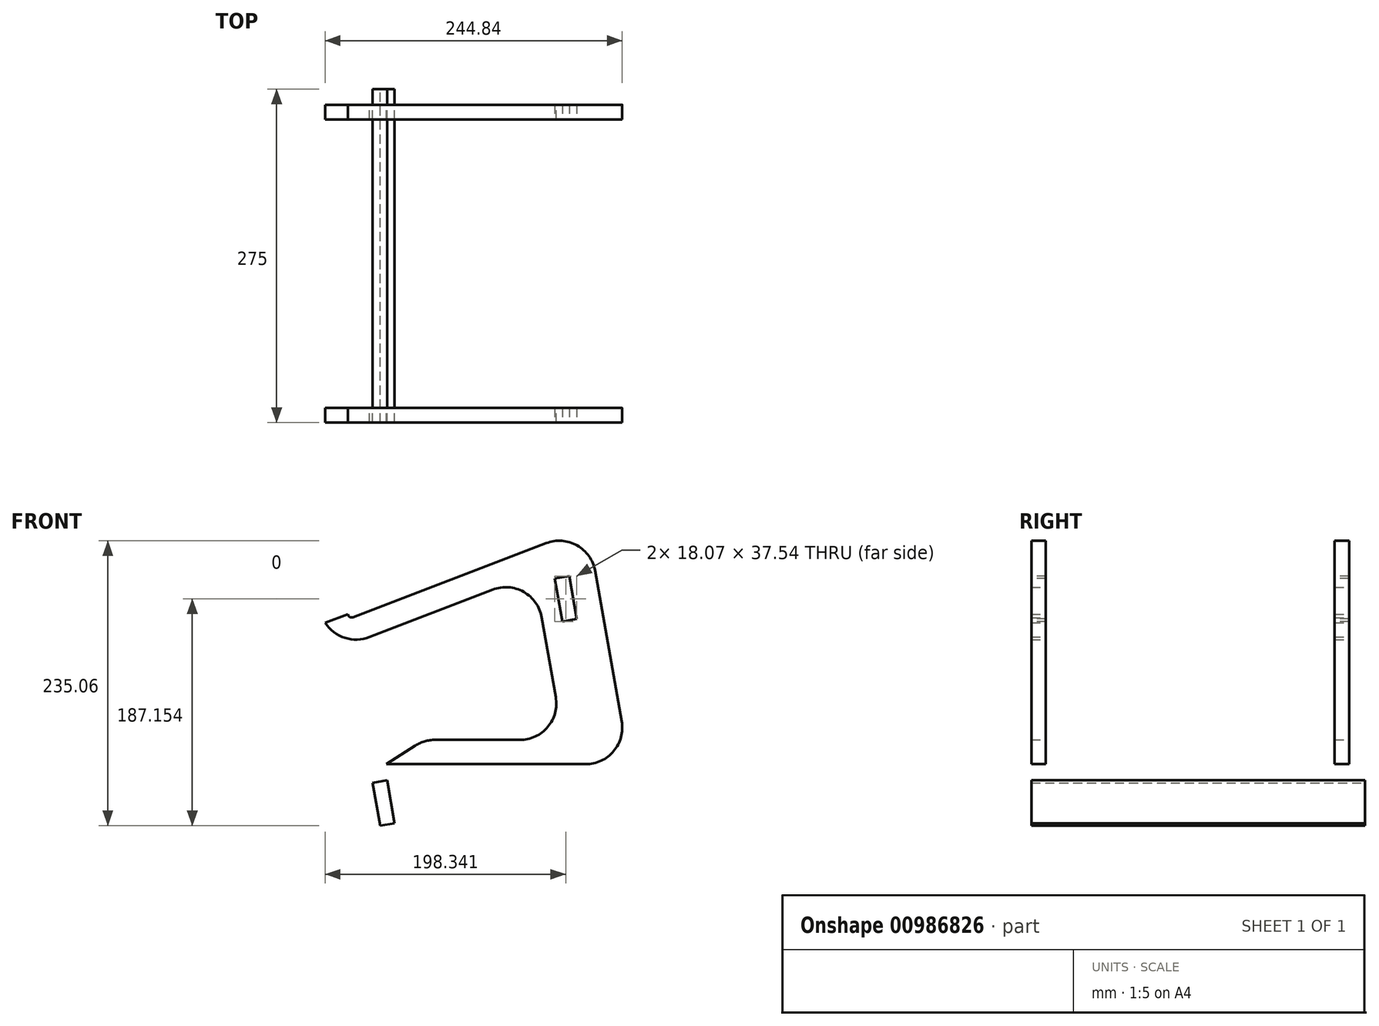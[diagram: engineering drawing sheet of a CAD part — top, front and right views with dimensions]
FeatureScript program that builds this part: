
annotation { "Feature Type Name" : "Feature", "Feature Type Description" : "" }
export const myFeature = defineFeature(function(context is Context, id is Id, definition is map)
    precondition{}
    {
        {
            var Q0;
            Q0=qCreatedBy(makeId("Front.planeOp"),FACE);
            var sketch = newSketch(context, id + "F0", { "sketchPlane" : qUnion([Q0])});
            skLineSegment(sketch, "E0", {"start": v(-177.62, 123.73) * mm, "end": v(-177.26, 122.8) * mm});
            skLineSegment(sketch, "E1", {"start": v(-173.38, 121.08) * mm, "end": v(-14.1, 182.22) * mm});
            skLineSegment(sketch, "E2", {"start": v(26.19, 159.42) * mm, "end": v(48.09, 35.2) * mm});
            skLineSegment(sketch, "E3", {"start": v(18.55, 0) * mm, "end": v(-145.7, 0) * mm});
            skLineSegment(sketch, "E4", {"start": v(-145.7, 0) * mm, "end": v(-121.89, 15.26) * mm});
            skLineSegment(sketch, "E5", {"start": v(-105.7, 20) * mm, "end": v(-35.75, 20) * mm});
            skLineSegment(sketch, "E6", {"start": v(-6.2, 55.2) * mm, "end": v(-17.83, 121.1) * mm});
            skLineSegment(sketch, "E7", {"start": v(-58.12, 143.9) * mm, "end": v(-159.68, 104.91) * mm});
            skPoint(sketch, "E8.visualSharp", {"position": v(-114.49, 20) * mm});
            skArc(sketch, "E8.filletArc", {"start": v(-105.7, 20) * mm, "mid": v(-114.13, 18.8) * mm, "end": v(-121.89, 15.26) * mm});
            skPoint(sketch, "E9.visualSharp", {"position": v(54.3, 0) * mm});
            skArc(sketch, "E9.filletArc", {"start": v(18.55, 0) * mm, "mid": v(41.53, 10.72) * mm, "end": v(48.09, 35.2) * mm});
            skPoint(sketch, "E10.visualSharp", {"position": v(0, 20) * mm});
            skArc(sketch, "E10.filletArc", {"start": v(-35.75, 20) * mm, "mid": v(-12.77, 30.72) * mm, "end": v(-6.2, 55.2) * mm});
            skPoint(sketch, "E11.visualSharp", {"position": v(-24.15, 156.94) * mm});
            skArc(sketch, "E11.filletArc", {"start": v(-17.83, 121.1) * mm, "mid": v(-32.6, 142) * mm, "end": v(-58.12, 143.9) * mm});
            skPoint(sketch, "E12.visualSharp", {"position": v(19.87, 195.26) * mm});
            skArc(sketch, "E12.filletArc", {"start": v(26.19, 159.42) * mm, "mid": v(11.42, 180.32) * mm, "end": v(-14.1, 182.22) * mm});
            skPoint(sketch, "E13.visualSharp", {"position": v(-187.69, 94.16) * mm});
            skPoint(sketch, "E14.visualSharp", {"position": v(-176.18, 120) * mm});
            skArc(sketch, "E14.filletArc", {"start": v(-177.26, 122.8) * mm, "mid": v(-175.68, 121.14) * mm, "end": v(-173.38, 121.08) * mm});
            skLineSegment(sketch, "E15", {"start": v(-196.29, 116.57) * mm, "end": v(-177.62, 123.73) * mm});
            skArc(sketch, "E16", {"start": v(-196.29, 116.57) * mm, "mid": v(-180.1, 104.11) * mm, "end": v(-159.68, 104.91) * mm});
            skSolve(sketch);
        }
        {
            var Q0;
            Q0=qSketchRegion(id+"F0",true);
            extrude(context, id + "F1", {"entities" : qUnion([Q0]), "depth" : 12 * mm, "offsetDistance" : 25 * mm});
        }
        {
            var Q0;
            Q0=makeQuery(id+"F1.opExtrude","CAP_FACE",FACE,{"disambiguationData":[OSD([sQuery(id+"F0.wireOp",EDGE,"E0"),sQuery(id+"F0.wireOp",EDGE,"E1"),sQuery(id+"F0.wireOp",EDGE,"E2"),sQuery(id+"F0.wireOp",EDGE,"E3"),sQuery(id+"F0.wireOp",EDGE,"E4"),sQuery(id+"F0.wireOp",EDGE,"E5"),sQuery(id+"F0.wireOp",EDGE,"E6"),sQuery(id+"F0.wireOp",EDGE,"E7"),sQuery(id+"F0.wireOp",EDGE,"E8.filletArc"),sQuery(id+"F0.wireOp",EDGE,"E9.filletArc"),sQuery(id+"F0.wireOp",EDGE,"E10.filletArc"),sQuery(id+"F0.wireOp",EDGE,"E11.filletArc"),sQuery(id+"F0.wireOp",EDGE,"E12.filletArc"),sQuery(id+"F0.wireOp",EDGE,"E14.filletArc"),sQuery(id+"F0.wireOp",EDGE,"E15"),sQuery(id+"F0.wireOp",EDGE,"E16")])],"isStart":false});
            var sketch = newSketch(context, id + "F2", { "sketchPlane" : qUnion([Q0])});
            skLineSegment(sketch, "E17.bottom", {"start": v(-6.98, 152.99) * mm, "end": v(4.83, 155.07) * mm});
            skLineSegment(sketch, "E17.top", {"start": v(-0.73, 117.54) * mm, "end": v(11.09, 119.62) * mm});
            skLineSegment(sketch, "E17.left", {"start": v(-6.98, 152.99) * mm, "end": v(-0.73, 117.54) * mm});
            skLineSegment(sketch, "E17.right", {"start": v(4.83, 155.07) * mm, "end": v(11.09, 119.62) * mm});
            skSolve(sketch);
        }
        {
            var Q0;
            Q0=qSketchRegion(id+"F2",true);
            extrude(context, id + "F3", {"entities" : qUnion([Q0]), "operationType" : NewBodyOperationType.REMOVE, "endBound" : BoundingType.THROUGH_ALL, "oppositeDirection" : true, "depth" : 25 * mm, "offsetDistance" : 25 * mm});
        }
        {
            var Q0;
            Q0=makeQuery(id+"F1.opExtrude","SWEPT_BODY",BODY,{"disambiguationData":[OSD([sQuery(id+"F0.wireOp",EDGE,"E0"),sQuery(id+"F0.wireOp",EDGE,"E1"),sQuery(id+"F0.wireOp",EDGE,"E2"),sQuery(id+"F0.wireOp",EDGE,"E3"),sQuery(id+"F0.wireOp",EDGE,"E4"),sQuery(id+"F0.wireOp",EDGE,"E5"),sQuery(id+"F0.wireOp",EDGE,"E6"),sQuery(id+"F0.wireOp",EDGE,"E7"),sQuery(id+"F0.wireOp",EDGE,"E8.filletArc"),sQuery(id+"F0.wireOp",EDGE,"E9.filletArc"),sQuery(id+"F0.wireOp",EDGE,"E10.filletArc"),sQuery(id+"F0.wireOp",EDGE,"E11.filletArc"),sQuery(id+"F0.wireOp",EDGE,"E12.filletArc"),sQuery(id+"F0.wireOp",EDGE,"E14.filletArc"),sQuery(id+"F0.wireOp",EDGE,"E15"),sQuery(id+"F0.wireOp",EDGE,"E16")])]});
            transform(context, id + "F4", {"entities" : qUnion([Q0]), "transformType" : TransformType.TRANSLATION_3D, "dx" : 0 * mm, "dy" : 250 * mm, "dz" : 0 * mm, "makeCopy" : true});
        }
        {
            var Q0;
            Q0=makeQuery(id+"F4.opPattern","COPY",FACE,{"derivedFrom":makeQuery(id+"F1.opExtrude","CAP_FACE",FACE,{"disambiguationData":[OSD([sQuery(id+"F0.wireOp",EDGE,"E0"),sQuery(id+"F0.wireOp",EDGE,"E1"),sQuery(id+"F0.wireOp",EDGE,"E2"),sQuery(id+"F0.wireOp",EDGE,"E3"),sQuery(id+"F0.wireOp",EDGE,"E4"),sQuery(id+"F0.wireOp",EDGE,"E5"),sQuery(id+"F0.wireOp",EDGE,"E6"),sQuery(id+"F0.wireOp",EDGE,"E7"),sQuery(id+"F0.wireOp",EDGE,"E8.filletArc"),sQuery(id+"F0.wireOp",EDGE,"E9.filletArc"),sQuery(id+"F0.wireOp",EDGE,"E10.filletArc"),sQuery(id+"F0.wireOp",EDGE,"E11.filletArc"),sQuery(id+"F0.wireOp",EDGE,"E12.filletArc"),sQuery(id+"F0.wireOp",EDGE,"E14.filletArc"),sQuery(id+"F0.wireOp",EDGE,"E15"),sQuery(id+"F0.wireOp",EDGE,"E16")])],"isStart":false}),"instanceName":"1"});
            var sketch = newSketch(context, id + "F5", { "sketchPlane" : qUnion([Q0])});
            skLineSegment(sketch, "E18.bottom", {"start": v(-157.12, -15.4) * mm, "end": v(-145.3, -13.31) * mm});
            skLineSegment(sketch, "E18.top", {"start": v(-150.87, -50.85) * mm, "end": v(-139.05, -48.77) * mm});
            skLineSegment(sketch, "E18.left", {"start": v(-157.12, -15.4) * mm, "end": v(-150.87, -50.85) * mm});
            skLineSegment(sketch, "E18.right", {"start": v(-145.3, -13.31) * mm, "end": v(-139.05, -48.77) * mm});
            skSolve(sketch);
        }
        {
            var Q0;
            Q0 = qSketchRegion(id + "F5", true);
            extrude(context, id + "F6", {"entities" : qUnion([Q0]), "depth" : 250 * mm, "offsetDistance" : 25 * mm});
        }
        {
            var Q0;
            Q0=makeQuery(id+"F6.opExtrude","CAP_FACE",FACE,{"disambiguationData":[OSD([sQuery(id+"F5.wireOp",EDGE,"E18.bottom"),sQuery(id+"F5.wireOp",EDGE,"E18.top"),sQuery(id+"F5.wireOp",EDGE,"E18.left"),sQuery(id+"F5.wireOp",EDGE,"E18.right")])],"isStart":true});
            extrude(context, id + "F7", {"entities" : qUnion([Q0]), "operationType" : NewBodyOperationType.ADD, "depth" : 25 * mm, "offsetDistance" : 25 * mm});
        }
    });
